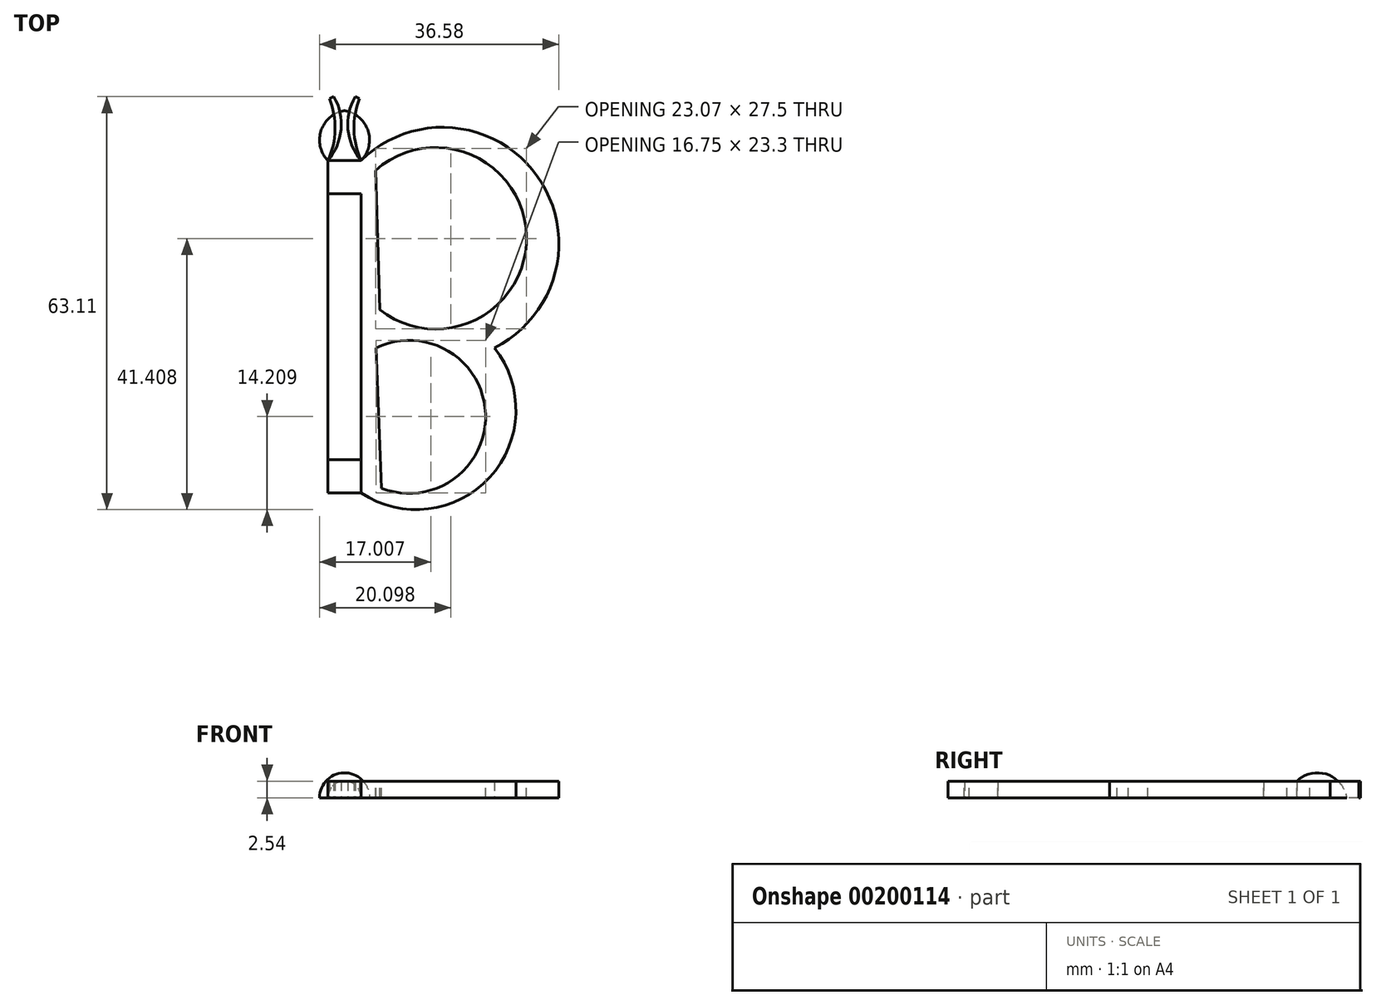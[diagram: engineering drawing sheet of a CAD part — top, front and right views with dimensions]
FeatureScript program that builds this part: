
annotation { "Feature Type Name" : "Feature", "Feature Type Description" : "" }
export const myFeature = defineFeature(function(context is Context, id is Id, definition is map)
    precondition{}
    {
        {
            var Q0;
            Q0=qCreatedBy(makeId("Top.planeOp"),FACE);
            var sketch = newSketch(context, id + "F0", { "sketchPlane" : qUnion([Q0])});
            skLineSegment(sketch, "E0.bottom", {"start": v(-2.54, 25.4) * mm, "end": v(2.54, 25.4) * mm});
            skLineSegment(sketch, "E0.top", {"start": v(-2.54, -25.4) * mm, "end": v(2.54, -25.4) * mm});
            skLineSegment(sketch, "E0.left", {"start": v(-2.54, 25.4) * mm, "end": v(-2.54, -25.4) * mm});
            skLineSegment(sketch, "E0.right", {"start": v(2.54, 25.4) * mm, "end": v(2.54, -25.4) * mm});
            skPoint(sketch, "E0.middle", {"position": v(0, 0) * mm});
            skLineSegment(sketch, "E1.top", {"start": v(-2.54, 20.32) * mm, "end": v(2.54, 20.32) * mm});
            skLineSegment(sketch, "E1.left", {"start": v(-2.54, 25.4) * mm, "end": v(-2.54, 20.32) * mm});
            skLineSegment(sketch, "E1.right", {"start": v(2.54, 25.4) * mm, "end": v(2.54, 20.32) * mm});
            skLineSegment(sketch, "E2.top", {"start": v(-2.54, -20.32) * mm, "end": v(2.54, -20.32) * mm});
            skLineSegment(sketch, "E2.left", {"start": v(-2.54, -25.4) * mm, "end": v(-2.54, -20.32) * mm});
            skLineSegment(sketch, "E2.right", {"start": v(2.54, -25.4) * mm, "end": v(2.54, -20.32) * mm});
            skSolve(sketch);
        }
        {
            var Q0;
            Q0=makeQuery(id+"F0.imprint","IMPRINT",FACE,{"disambiguationData":[TD([[makeQuery(id+"F0.imprint","IMPRINT",EDGE,{"derivedFrom":sQuery(id+"F0.wireOp",EDGE,"E0.bottom")}),-1.0]])]});
            var Q1;
            Q1=makeQuery(id+"F0.imprint","IMPRINT",FACE,{"disambiguationData":[TD([[makeQuery(id+"F0.imprint","IMPRINT",EDGE,{"derivedFrom":sQuery(id+"F0.wireOp",EDGE,"E0.top")}),1.0]])]});
            extrude(context, id + "F1", {"entities" : qUnion([Q0, Q1]), "depth" : 2.54 * mm});
        }
        {
            var Q0;
            Q0=makeQuery(id+"F1.opExtrude","SWEPT_FACE",FACE,{"disambiguationData":[OSD([sQuery(id+"F0.wireOp",EDGE,"E1.top")])]});
            var sketch = newSketch(context, id + "F2", { "sketchPlane" : qUnion([Q0])});
            skArc(sketch, "E3", {"start": v(2.54, 0) * mm, "mid": v(0, 2.54) * mm, "end": v(-2.54, 0) * mm});
            skSolve(sketch);
        }
        {
            var Q0;
            {var subQ1=sQuery(id+"F0.wireOp",EDGE,"E1.top");var subQ2=makeQuery(id+"F1.opExtrude","CAP_EDGE",EDGE,{"disambiguationData":[OSD([subQ1])],"isStart":true});Q0=makeQuery(id+"F2.imprint","IMPRINT",FACE,{"disambiguationData":[TD([[makeQuery(id+"F2.imprint","IMPRINT",EDGE,{"derivedFrom":subQ2}),1.0]])]});}
            extrude(context, id + "F3", {"entities" : qUnion([Q0]), "depth" : 40.64 * mm});
        }
        {
            var Q0;
            Q0=qCreatedBy(makeId("Top.planeOp"),FACE);
            var sketch = newSketch(context, id + "F4", { "sketchPlane" : qUnion([Q0])});
            skArc(sketch, "E4", {"start": v(2.54, 0) * mm, "mid": v(32.76, 12.7) * mm, "end": v(2.54, 25.4) * mm});
            skArc(sketch, "E5", {"start": v(2.54, -25.4) * mm, "mid": v(26.2, -12.7) * mm, "end": v(2.54, 0) * mm});
            skLineSegment(sketch, "E6", {"start": v(2.54, 25.4) * mm, "end": v(2.54, -25.4) * mm});
            skArc(sketch, "E7.MirrorCS", {"start": v(-2.54, 0) * mm, "mid": v(-32.76, 12.7) * mm, "end": v(-2.54, 25.4) * mm});
            skArc(sketch, "E8.MirrorCS", {"start": v(-2.54, -25.4) * mm, "mid": v(-26.2, -12.7) * mm, "end": v(-2.54, 0) * mm});
            skLineSegment(sketch, "E9.MirrorCS", {"start": v(-2.54, 25.4) * mm, "end": v(-2.54, -25.4) * mm});
            skSolve(sketch);
        }
        {
            var Q0;
            {var subQ0=sQuery(id+"F4.wireOp",EDGE,"E6");var subQ1=sQuery(id+"F4.wireOp",EDGE,"E4");var subQ2=makeQuery(id+"F4.imprint","INTERSECT",VERTEX,{"derivedFrom":[subQ1,subQ0]});Q0=makeQuery(id+"F4.imprint","IMPRINT",FACE,{"disambiguationData":[TD([[makeQuery(id+"F4.imprint","IMPRINT",EDGE,{"disambiguationData":[TD([[subQ2,1.0]])],"derivedFrom":subQ1}),1.0]])]});}
            var Q1;
            {var subQ0=sQuery(id+"F4.wireOp",EDGE,"E6");var subQ1=sQuery(id+"F4.wireOp",EDGE,"E5");var subQ5=makeQuery(id+"F4.imprint","INTERSECT",VERTEX,{"derivedFrom":[subQ1,subQ0]});Q1=makeQuery(id+"F4.imprint","IMPRINT",FACE,{"disambiguationData":[TD([[makeQuery(id+"F4.imprint","IMPRINT",EDGE,{"disambiguationData":[TD([[subQ5,-1.0]])],"derivedFrom":subQ1}),1.0]])]});}
            var Q2;
            {var subQ0=sQuery(id+"F4.wireOp",EDGE,"E5");var subQ1=sQuery(id+"F4.wireOp",EDGE,"E4");var subQ3=makeQuery(id+"F4.imprint","INTERSECT",VERTEX,{"derivedFrom":[subQ1,subQ0]});Q2=makeQuery(id+"F4.imprint","IMPRINT",FACE,{"disambiguationData":[TD([[makeQuery(id+"F4.imprint","IMPRINT",EDGE,{"disambiguationData":[TD([[subQ3,1.0]])],"derivedFrom":subQ1}),1.0]])]});}
            var Q3;
            {var subQ0=sQuery(id+"F4.wireOp",EDGE,"E9.MirrorCS");var subQ1=sQuery(id+"F4.wireOp",EDGE,"E7.MirrorCS");var subQ2=makeQuery(id+"F4.imprint","INTERSECT",VERTEX,{"derivedFrom":[subQ1,subQ0]});Q3=makeQuery(id+"F4.imprint","IMPRINT",FACE,{"disambiguationData":[TD([[makeQuery(id+"F4.imprint","IMPRINT",EDGE,{"disambiguationData":[TD([[subQ2,1.0]])],"derivedFrom":subQ1}),-1.0]])]});}
            var Q4;
            {var subQ0=sQuery(id+"F4.wireOp",EDGE,"E8.MirrorCS");var subQ1=sQuery(id+"F4.wireOp",EDGE,"E7.MirrorCS");var subQ3=makeQuery(id+"F4.imprint","INTERSECT",VERTEX,{"derivedFrom":[subQ1,subQ0]});Q4=makeQuery(id+"F4.imprint","IMPRINT",FACE,{"disambiguationData":[TD([[makeQuery(id+"F4.imprint","IMPRINT",EDGE,{"disambiguationData":[TD([[subQ3,1.0]])],"derivedFrom":subQ1}),-1.0]])]});}
            var Q5;
            {var subQ0=sQuery(id+"F4.wireOp",EDGE,"E9.MirrorCS");var subQ1=sQuery(id+"F4.wireOp",EDGE,"E8.MirrorCS");var subQ5=makeQuery(id+"F4.imprint","INTERSECT",VERTEX,{"derivedFrom":[subQ1,subQ0]});Q5=makeQuery(id+"F4.imprint","IMPRINT",FACE,{"disambiguationData":[TD([[makeQuery(id+"F4.imprint","IMPRINT",EDGE,{"disambiguationData":[TD([[subQ5,-1.0]])],"derivedFrom":subQ1}),-1.0]])]});}
            extrude(context, id + "F5", {"entities" : qUnion([Q0, Q1, Q2, Q3, Q4, Q5]), "depth" : 2.54 * mm});
        }
        {
            var Q0;
            Q0=qCreatedBy(makeId("Top.planeOp"),FACE);
            var sketch = newSketch(context, id + "F6", { "sketchPlane" : qUnion([Q0])});
            skLineSegment(sketch, "E10", {"start": v(0, 25.4) * mm, "end": v(0, 33.02) * mm});
            skArc(sketch, "E11", {"start": v(0, 33.02) * mm, "mid": v(-3.58, 29.98) * mm, "end": v(-2.54, 25.4) * mm});
            skLineSegment(sketch, "E12", {"start": v(-2.54, 25.4) * mm, "end": v(0, 25.4) * mm});
            skSolve(sketch);
        }
        {
            var Q0;
            Q0=makeQuery(id+"F6.imprint","IMPRINT",FACE,{"disambiguationData":[TD([[makeQuery(id+"F6.imprint","IMPRINT",EDGE,{"derivedFrom":sQuery(id+"F6.wireOp",EDGE,"E10")}),1.0]])]});
            var Q1;
            Q1=sQuery(id+"F6.wireOp",EDGE,"E10");
            revolve(context, id + "F7", {"operationType" : NewBodyOperationType.ADD, "entities" : qUnion([Q0]), "axis" : qUnion([Q1]), "revolveType" : RevolveType.ONE_DIRECTION, "angle" : 180 * degree});
        }
        {
            var Q0;
            Q0=makeQuery(id+"F7.boolean.opBoolean","MERGE",FACE,{"derivedFrom":[makeQuery(id+"F1.opExtrude","CAP_FACE",FACE,{"disambiguationData":[OSD([sQuery(id+"F0.wireOp",EDGE,"E0.bottom"),sQuery(id+"F0.wireOp",EDGE,"E1.top"),sQuery(id+"F0.wireOp",EDGE,"E1.left"),sQuery(id+"F0.wireOp",EDGE,"E1.right")])],"isStart":false}),makeQuery(id+"F5.opExtrude","CAP_FACE",FACE,{"disambiguationData":[OSD([sQuery(id+"F4.wireOp",EDGE,"E4"),sQuery(id+"F4.wireOp",EDGE,"E5"),sQuery(id+"F4.wireOp",EDGE,"E6")])],"isStart":false}),makeQuery(id+"F5.opExtrude","CAP_FACE",FACE,{"disambiguationData":[OSD([sQuery(id+"F4.wireOp",EDGE,"E7.MirrorCS"),sQuery(id+"F4.wireOp",EDGE,"E8.MirrorCS"),sQuery(id+"F4.wireOp",EDGE,"E9.MirrorCS")])],"isStart":false})]});
            var sketch = newSketch(context, id + "F8", { "sketchPlane" : qUnion([Q0])});
            skArc(sketch, "E13", {"start": v(-4.74, 23.9) * mm, "mid": v(-27.81, 13.93) * mm, "end": v(-5.37, 2.61) * mm});
            skArc(sketch, "E14", {"start": v(-4.81, -3.22) * mm, "mid": v(-21.56, -13.32) * mm, "end": v(-5.63, -24.68) * mm});
            skLineSegment(sketch, "E15", {"start": v(-4.81, -3.22) * mm, "end": v(-5.63, -24.68) * mm});
            skLineSegment(sketch, "E16", {"start": v(-4.74, 23.9) * mm, "end": v(-5.37, 2.61) * mm});
            skLineSegment(sketch, "E17.MirrorCS", {"start": v(4.74, 23.9) * mm, "end": v(5.37, 2.61) * mm});
            skArc(sketch, "E18.MirrorCS", {"start": v(4.74, 23.9) * mm, "mid": v(27.81, 13.93) * mm, "end": v(5.37, 2.61) * mm});
            skLineSegment(sketch, "E19.MirrorCS", {"start": v(4.81, -3.22) * mm, "end": v(5.63, -24.68) * mm});
            skArc(sketch, "E20.MirrorCS", {"start": v(4.81, -3.22) * mm, "mid": v(21.56, -13.32) * mm, "end": v(5.63, -24.68) * mm});
            skSolve(sketch);
        }
        {
            var Q0;
            Q0=makeQuery(id+"F8.imprint","IMPRINT",FACE,{"disambiguationData":[TD([[makeQuery(id+"F8.imprint","IMPRINT",EDGE,{"derivedFrom":sQuery(id+"F8.wireOp",EDGE,"E17.MirrorCS")}),1.0]])]});
            var Q1;
            Q1=makeQuery(id+"F8.imprint","IMPRINT",FACE,{"disambiguationData":[TD([[makeQuery(id+"F8.imprint","IMPRINT",EDGE,{"derivedFrom":sQuery(id+"F8.wireOp",EDGE,"E19.MirrorCS")}),1.0]])]});
            var Q2;
            Q2=makeQuery(id+"F8.imprint","IMPRINT",FACE,{"disambiguationData":[TD([[makeQuery(id+"F8.imprint","IMPRINT",EDGE,{"derivedFrom":sQuery(id+"F8.wireOp",EDGE,"E14")}),1.0]])]});
            var Q3;
            Q3=makeQuery(id+"F8.imprint","IMPRINT",FACE,{"disambiguationData":[TD([[makeQuery(id+"F8.imprint","IMPRINT",EDGE,{"derivedFrom":sQuery(id+"F8.wireOp",EDGE,"E13")}),1.0]])]});
            extrude(context, id + "F9", {"entities" : qUnion([Q0, Q1, Q2, Q3]), "operationType" : NewBodyOperationType.REMOVE, "endBound" : BoundingType.THROUGH_ALL, "oppositeDirection" : true, "depth" : 25.4 * mm});
        }
        {
            var Q0;
            Q0=makeQuery(id+"F7.boolean.opBoolean","MERGE",FACE,{"derivedFrom":[makeQuery(id+"F1.opExtrude","CAP_FACE",FACE,{"disambiguationData":[OSD([sQuery(id+"F0.wireOp",EDGE,"E0.bottom"),sQuery(id+"F0.wireOp",EDGE,"E1.top"),sQuery(id+"F0.wireOp",EDGE,"E1.left"),sQuery(id+"F0.wireOp",EDGE,"E1.right")])],"isStart":true}),makeQuery(id+"F5.opExtrude","CAP_FACE",FACE,{"disambiguationData":[OSD([sQuery(id+"F4.wireOp",EDGE,"E4"),sQuery(id+"F4.wireOp",EDGE,"E5"),sQuery(id+"F4.wireOp",EDGE,"E6")])],"isStart":true}),makeQuery(id+"F5.opExtrude","CAP_FACE",FACE,{"disambiguationData":[OSD([sQuery(id+"F4.wireOp",EDGE,"E7.MirrorCS"),sQuery(id+"F4.wireOp",EDGE,"E8.MirrorCS"),sQuery(id+"F4.wireOp",EDGE,"E9.MirrorCS")])],"isStart":true}),makeQuery(id+"F7.opRevolve","CAP_FACE",FACE,{"disambiguationData":[OSD([sQuery(id+"F6.wireOp",EDGE,"E10"),sQuery(id+"F6.wireOp",EDGE,"E11"),sQuery(id+"F6.wireOp",EDGE,"E12")])],"isStart":true})]});
            var sketch = newSketch(context, id + "F10", { "sketchPlane" : qUnion([Q0])});
            skArc(sketch, "E21", {"start": v(2.54, -25.4) * mm, "mid": v(0.53, -30.14) * mm, "end": v(1.62, -35.17) * mm});
            skArc(sketch, "E22", {"start": v(2.54, -25.4) * mm, "mid": v(1.44, -30.11) * mm, "end": v(2.31, -34.88) * mm});
            skLineSegment(sketch, "E23", {"start": v(1.62, -35.17) * mm, "end": v(2.31, -34.88) * mm});
            skArc(sketch, "E24.MirrorCS", {"start": v(-2.54, -25.4) * mm, "mid": v(-1.44, -30.11) * mm, "end": v(-2.31, -34.88) * mm});
            skLineSegment(sketch, "E25.MirrorCS", {"start": v(-1.62, -35.17) * mm, "end": v(-2.31, -34.88) * mm});
            skArc(sketch, "E26.MirrorCS", {"start": v(-2.54, -25.4) * mm, "mid": v(-0.53, -30.14) * mm, "end": v(-1.62, -35.17) * mm});
            skSolve(sketch);
        }
        {
            var Q0;
            Q0 = qSketchRegion(id + "F10", true);
            extrude(context, id + "F11", {"entities" : qUnion([Q0]), "oppositeDirection" : true, "depth" : 2.54 * mm});
        }
    });
